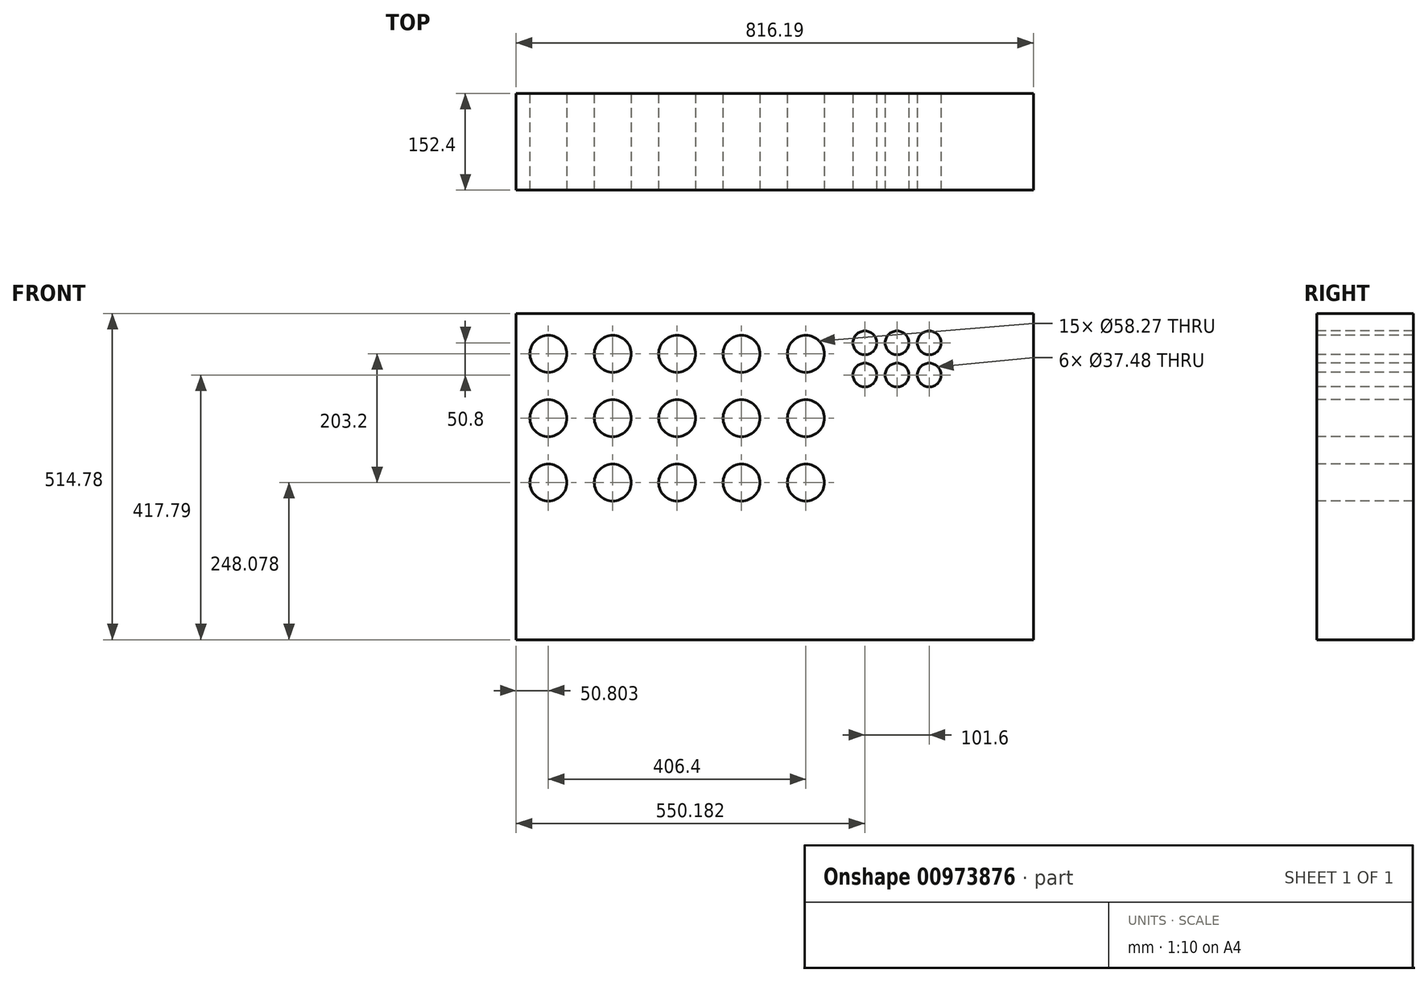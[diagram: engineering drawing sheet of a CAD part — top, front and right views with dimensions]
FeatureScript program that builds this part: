
annotation { "Feature Type Name" : "Feature", "Feature Type Description" : "" }
export const myFeature = defineFeature(function(context is Context, id is Id, definition is map)
    precondition{}
    {
        {
            var Q0;
            Q0=qCreatedBy(makeId("Front.planeOp"),FACE);
            var sketch = newSketch(context, id + "F0", { "sketchPlane" : qUnion([Q0])});
            skLineSegment(sketch, "E0.bottom", {"start": v(-399.8, 258.65) * mm, "end": v(416.38, 258.65) * mm});
            skLineSegment(sketch, "E0.top", {"start": v(-399.8, -256.13) * mm, "end": v(416.38, -256.13) * mm});
            skLineSegment(sketch, "E0.left", {"start": v(-399.8, 258.65) * mm, "end": v(-399.8, -256.13) * mm});
            skLineSegment(sketch, "E0.right", {"start": v(416.38, 258.65) * mm, "end": v(416.38, -256.13) * mm});
            skCircle(sketch, "E1", {"center": v(-349, 195.15) * mm, "radius": 29.13 * mm});
            skCircle(sketch, "E2.0.1.0", {"center": v(-349, 93.55) * mm, "radius": 29.13 * mm});
            skCircle(sketch, "E2.0.2.0", {"center": v(-349, -8.05) * mm, "radius": 29.13 * mm});
            skCircle(sketch, "E2.1.0.0", {"center": v(-247.4, 195.15) * mm, "radius": 29.13 * mm});
            skCircle(sketch, "E2.1.1.0", {"center": v(-247.4, 93.55) * mm, "radius": 29.13 * mm});
            skCircle(sketch, "E2.1.2.0", {"center": v(-247.4, -8.05) * mm, "radius": 29.13 * mm});
            skCircle(sketch, "E2.2.0.0", {"center": v(-145.8, 195.15) * mm, "radius": 29.13 * mm});
            skCircle(sketch, "E2.2.1.0", {"center": v(-145.8, 93.55) * mm, "radius": 29.13 * mm});
            skCircle(sketch, "E2.2.2.0", {"center": v(-145.8, -8.05) * mm, "radius": 29.13 * mm});
            skCircle(sketch, "E2.3.0.0", {"center": v(-44.2, 195.15) * mm, "radius": 29.13 * mm});
            skCircle(sketch, "E2.3.1.0", {"center": v(-44.2, 93.55) * mm, "radius": 29.13 * mm});
            skCircle(sketch, "E2.3.2.0", {"center": v(-44.2, -8.05) * mm, "radius": 29.13 * mm});
            skCircle(sketch, "E2.4.0.0", {"center": v(57.4, 195.15) * mm, "radius": 29.13 * mm});
            skCircle(sketch, "E2.4.1.0", {"center": v(57.4, 93.55) * mm, "radius": 29.13 * mm});
            skCircle(sketch, "E2.4.2.0", {"center": v(57.4, -8.05) * mm, "radius": 29.13 * mm});
            skLineSegment(sketch, "E2.direction1", {"start": v(-349, 195.15) * mm, "end": v(-247.4, 195.15) * mm, "construction": true});
            skLineSegment(sketch, "E2.direction2", {"start": v(-349, 195.15) * mm, "end": v(-349, 93.55) * mm, "construction": true});
            skCircle(sketch, "E3", {"center": v(150.37, 212.46) * mm, "radius": 18.74 * mm});
            skCircle(sketch, "E4.0.1.0", {"center": v(150.37, 161.66) * mm, "radius": 18.74 * mm});
            skCircle(sketch, "E4.1.0.0", {"center": v(201.17, 212.46) * mm, "radius": 18.74 * mm});
            skCircle(sketch, "E4.1.1.0", {"center": v(201.17, 161.66) * mm, "radius": 18.74 * mm});
            skCircle(sketch, "E4.2.0.0", {"center": v(251.97, 212.46) * mm, "radius": 18.74 * mm});
            skCircle(sketch, "E4.2.1.0", {"center": v(251.97, 161.66) * mm, "radius": 18.74 * mm});
            skLineSegment(sketch, "E4.direction1", {"start": v(150.37, 212.46) * mm, "end": v(201.17, 212.46) * mm, "construction": true});
            skLineSegment(sketch, "E4.direction2", {"start": v(150.37, 212.46) * mm, "end": v(150.37, 161.66) * mm, "construction": true});
            skSolve(sketch);
        }
        {
            var Q0;
            Q0=makeQuery(id+"F0.imprint","IMPRINT",FACE,{"disambiguationData":[TD([[makeQuery(id+"F0.imprint","IMPRINT",EDGE,{"derivedFrom":sQuery(id+"F0.wireOp",EDGE,"E0.bottom")}),-1.0]])]});
            extrude(context, id + "F1", {"entities" : qUnion([Q0]), "oppositeDirection" : true, "depth" : 127 * mm, "offsetDistance" : 25.4 * mm});
        }
        {
            var Q0;
            Q0=makeQuery(id+"F1.opExtrude","CAP_FACE",FACE,{"disambiguationData":[OSD([sQuery(id+"F0.wireOp",EDGE,"E0.bottom"),sQuery(id+"F0.wireOp",EDGE,"E0.top"),sQuery(id+"F0.wireOp",EDGE,"E0.left"),sQuery(id+"F0.wireOp",EDGE,"E0.right"),sQuery(id+"F0.wireOp",EDGE,"E1"),sQuery(id+"F0.wireOp",EDGE,"E2.0.1.0"),sQuery(id+"F0.wireOp",EDGE,"E2.0.2.0"),sQuery(id+"F0.wireOp",EDGE,"E2.1.0.0"),sQuery(id+"F0.wireOp",EDGE,"E2.1.1.0"),sQuery(id+"F0.wireOp",EDGE,"E2.1.2.0"),sQuery(id+"F0.wireOp",EDGE,"E2.2.0.0"),sQuery(id+"F0.wireOp",EDGE,"E2.2.1.0"),sQuery(id+"F0.wireOp",EDGE,"E2.2.2.0"),sQuery(id+"F0.wireOp",EDGE,"E2.3.0.0"),sQuery(id+"F0.wireOp",EDGE,"E2.3.1.0"),sQuery(id+"F0.wireOp",EDGE,"E2.3.2.0"),sQuery(id+"F0.wireOp",EDGE,"E2.4.0.0"),sQuery(id+"F0.wireOp",EDGE,"E2.4.1.0"),sQuery(id+"F0.wireOp",EDGE,"E2.4.2.0"),sQuery(id+"F0.wireOp",EDGE,"E3"),sQuery(id+"F0.wireOp",EDGE,"E4.0.1.0"),sQuery(id+"F0.wireOp",EDGE,"E4.1.0.0"),sQuery(id+"F0.wireOp",EDGE,"E4.1.1.0"),sQuery(id+"F0.wireOp",EDGE,"E4.2.0.0"),sQuery(id+"F0.wireOp",EDGE,"E4.2.1.0")])],"isStart":true});
            extrude(context, id + "F2", {"entities" : qUnion([Q0]), "operationType" : NewBodyOperationType.ADD, "depth" : 25.4 * mm, "offsetDistance" : 25.4 * mm});
        }
    });
